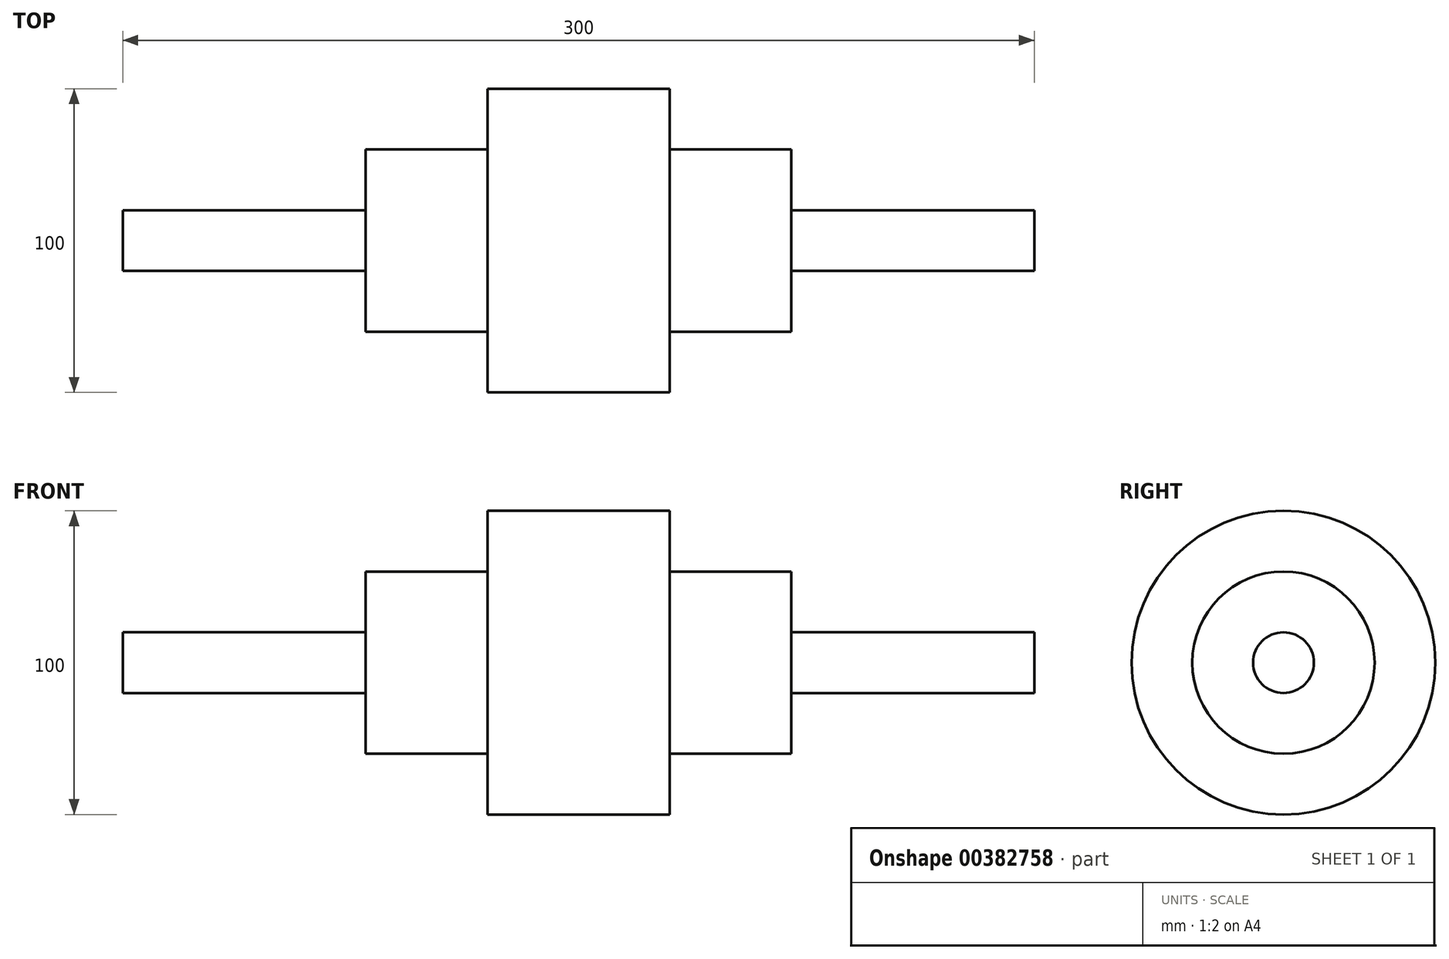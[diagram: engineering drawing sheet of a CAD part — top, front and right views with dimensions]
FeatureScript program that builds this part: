
annotation { "Feature Type Name" : "Feature", "Feature Type Description" : "" }
export const myFeature = defineFeature(function(context is Context, id is Id, definition is map)
    precondition{}
    {
        {
            var Q0;
            Q0=qCreatedBy(makeId("Front.planeOp"),FACE);
            var sketch = newSketch(context, id + "F0", { "sketchPlane" : qUnion([Q0])});
            skLineSegment(sketch, "E0", {"start": v(-150, 0) * mm, "end": v(150, 0) * mm, "construction": true});
            skLineSegment(sketch, "E1.bottom", {"start": v(-150, 0) * mm, "end": v(-70, 0) * mm});
            skLineSegment(sketch, "E1.top", {"start": v(-150, 10) * mm, "end": v(-70, 10) * mm});
            skLineSegment(sketch, "E1.left", {"start": v(-150, 0) * mm, "end": v(-150, 10) * mm});
            skLineSegment(sketch, "E1.right", {"start": v(-70, 0) * mm, "end": v(-70, 10) * mm});
            skLineSegment(sketch, "E2.bottom", {"start": v(-70, 0) * mm, "end": v(-30, 0) * mm});
            skLineSegment(sketch, "E2.top", {"start": v(-70, 30) * mm, "end": v(-30, 30) * mm});
            skLineSegment(sketch, "E2.left", {"start": v(-70, 0) * mm, "end": v(-70, 30) * mm});
            skLineSegment(sketch, "E2.right", {"start": v(-30, 0) * mm, "end": v(-30, 30) * mm});
            skLineSegment(sketch, "E3.bottom", {"start": v(-30, 0) * mm, "end": v(30, 0) * mm});
            skLineSegment(sketch, "E3.top", {"start": v(-30, 50) * mm, "end": v(30, 50) * mm});
            skLineSegment(sketch, "E3.left", {"start": v(-30, 0) * mm, "end": v(-30, 50) * mm});
            skLineSegment(sketch, "E3.right", {"start": v(30, 0) * mm, "end": v(30, 50) * mm});
            skLineSegment(sketch, "E4.bottom", {"start": v(30, 0) * mm, "end": v(70, 0) * mm});
            skLineSegment(sketch, "E4.top", {"start": v(30, 30) * mm, "end": v(70, 30) * mm});
            skLineSegment(sketch, "E4.left", {"start": v(30, 0) * mm, "end": v(30, 30) * mm});
            skLineSegment(sketch, "E4.right", {"start": v(70, 0) * mm, "end": v(70, 30) * mm});
            skLineSegment(sketch, "E5.bottom", {"start": v(70, 0) * mm, "end": v(150, 0) * mm});
            skLineSegment(sketch, "E5.top", {"start": v(70, 10) * mm, "end": v(150, 10) * mm});
            skLineSegment(sketch, "E5.left", {"start": v(70, 0) * mm, "end": v(70, 10) * mm});
            skLineSegment(sketch, "E5.right", {"start": v(150, 0) * mm, "end": v(150, 10) * mm});
            skSolve(sketch);
        }
        {
            var Q0;
            {var subQ0=sQuery(id+"F0.wireOp",EDGE,"E1.bottom");Q0=makeQuery(id+"F0.imprint","IMPRINT",FACE,{"disambiguationData":[TD([[makeQuery(id+"F0.imprint","IMPRINT",EDGE,{"derivedFrom":subQ0}),1.0]])]});}
            var Q1;
            {var subQ3=sQuery(id+"F0.wireOp",EDGE,"E2.bottom");Q1=makeQuery(id+"F0.imprint","IMPRINT",FACE,{"disambiguationData":[TD([[makeQuery(id+"F0.imprint","IMPRINT",EDGE,{"derivedFrom":subQ3}),1.0]])]});}
            var Q2;
            {var subQ3=sQuery(id+"F0.wireOp",EDGE,"E3.bottom");Q2=makeQuery(id+"F0.imprint","IMPRINT",FACE,{"disambiguationData":[TD([[makeQuery(id+"F0.imprint","IMPRINT",EDGE,{"derivedFrom":subQ3}),1.0]])]});}
            var Q3;
            Q3=makeQuery(id+"F0.imprint","IMPRINT",FACE,{"disambiguationData":[TD([[makeQuery(id+"F0.imprint","IMPRINT",EDGE,{"derivedFrom":sQuery(id+"F0.wireOp",EDGE,"E4.bottom")}),1.0]])]});
            var Q4;
            Q4=makeQuery(id+"F0.imprint","IMPRINT",FACE,{"disambiguationData":[TD([[makeQuery(id+"F0.imprint","IMPRINT",EDGE,{"derivedFrom":sQuery(id+"F0.wireOp",EDGE,"E5.bottom")}),1.0]])]});
            var Q5;
            Q5=sQuery(id+"F0.wireOp",EDGE,"E3.bottom");
            revolve(context, id + "F1", {"entities" : qUnion([Q0, Q1, Q2, Q3, Q4]), "axis" : qUnion([Q5]), "revolveType" : RevolveType.FULL});
        }
    });
